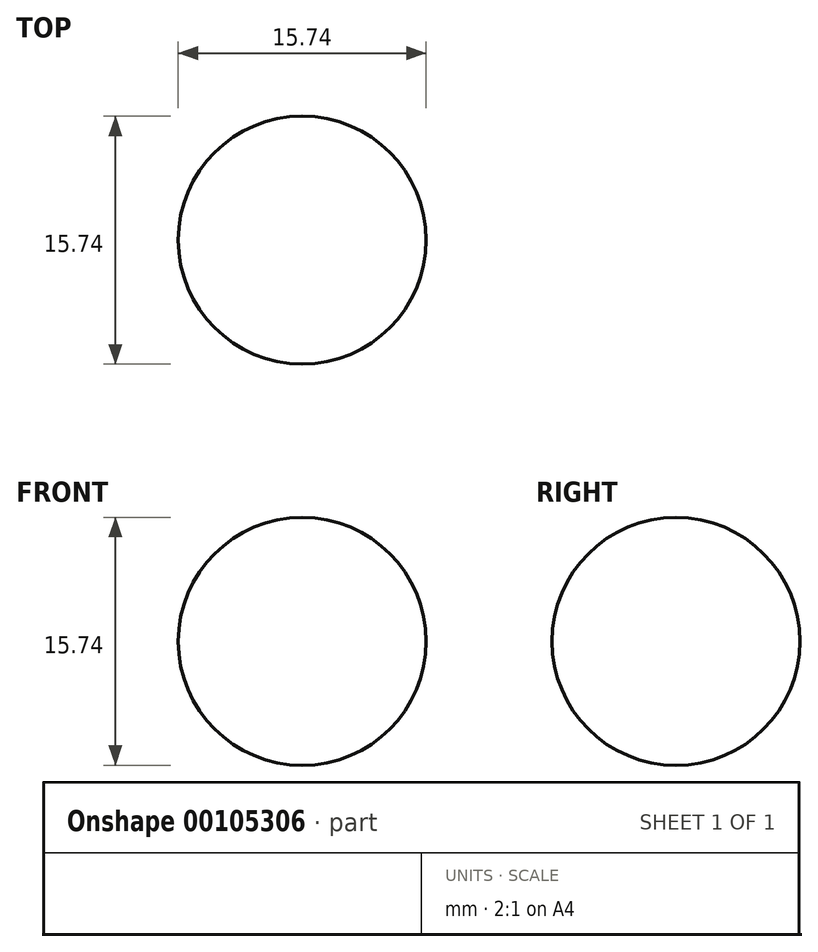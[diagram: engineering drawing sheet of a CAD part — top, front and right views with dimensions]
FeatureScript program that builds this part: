
annotation { "Feature Type Name" : "Feature", "Feature Type Description" : "" }
export const myFeature = defineFeature(function(context is Context, id is Id, definition is map)
    precondition{}
    {
        {
            var Q0;
            Q0=qCreatedBy(makeId("Front.planeOp"),FACE);
            var sketch = newSketch(context, id + "F0", { "sketchPlane" : qUnion([Q0])});
            skLineSegment(sketch, "E0", {"start": v(15.24, 5.55) * mm, "end": v(15.24, -10.2) * mm});
            skArc(sketch, "E1", {"start": v(7.37, -2.32) * mm, "mid": v(9.67, -7.89) * mm, "end": v(15.24, -10.2) * mm});
            skPoint(sketch, "E1.startSnap0", {"position": v(15.24, -2.32) * mm});
            skArc(sketch, "E2", {"start": v(7.37, -2.32) * mm, "mid": v(9.67, 3.25) * mm, "end": v(15.24, 5.55) * mm});
            skSolve(sketch);
        }
        {
            var Q0;
            Q0=makeQuery(id+"F0.imprint","IMPRINT",FACE,{"disambiguationData":[TD([[makeQuery(id+"F0.imprint","IMPRINT",EDGE,{"derivedFrom":sQuery(id+"F0.wireOp",EDGE,"E0")}),-1.0]])]});
            var Q1;
            Q1=sQuery(id+"F0.wireOp",EDGE,"E0");
            revolve(context, id + "F1", {"entities" : qUnion([Q0]), "axis" : qUnion([Q1]), "revolveType" : RevolveType.FULL});
        }
    });
